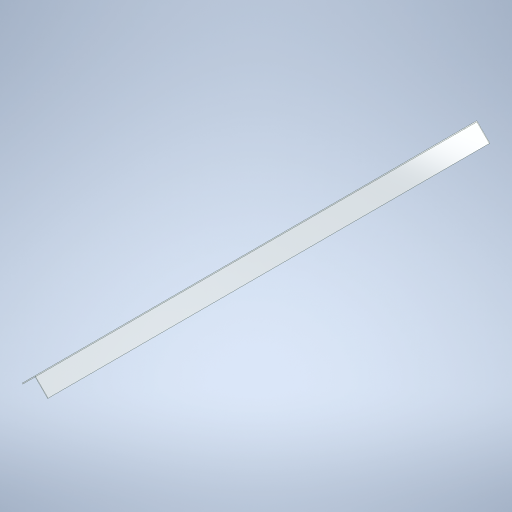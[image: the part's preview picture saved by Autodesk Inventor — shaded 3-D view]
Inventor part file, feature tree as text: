
AUTODESK INVENTOR PART (.ipt)
format: ipt  version: 2024 (Build 280153000, 153)  size: 254,464 bytes
history: native  units: in
note: dims shown in document units (in); Inventor stores cm internally (conversion verified against a paired STEP export)
features: extrude x1, sketch x1
ambient origin geometry x8: Origin, YZ Plane, XZ Plane, XY Plane, X Axis, Y Axis, Z Axis, Center Point
bodies: Solid1 (feature_tree)
feature tree (2):
  extrude  "Extrusion1"  Depth=300.0in TaperAngle=0.0deg
  sketch  "Sketch1"  dims[d0=0.5in d2=300.0in d3=0.0in d4=12.0in]
